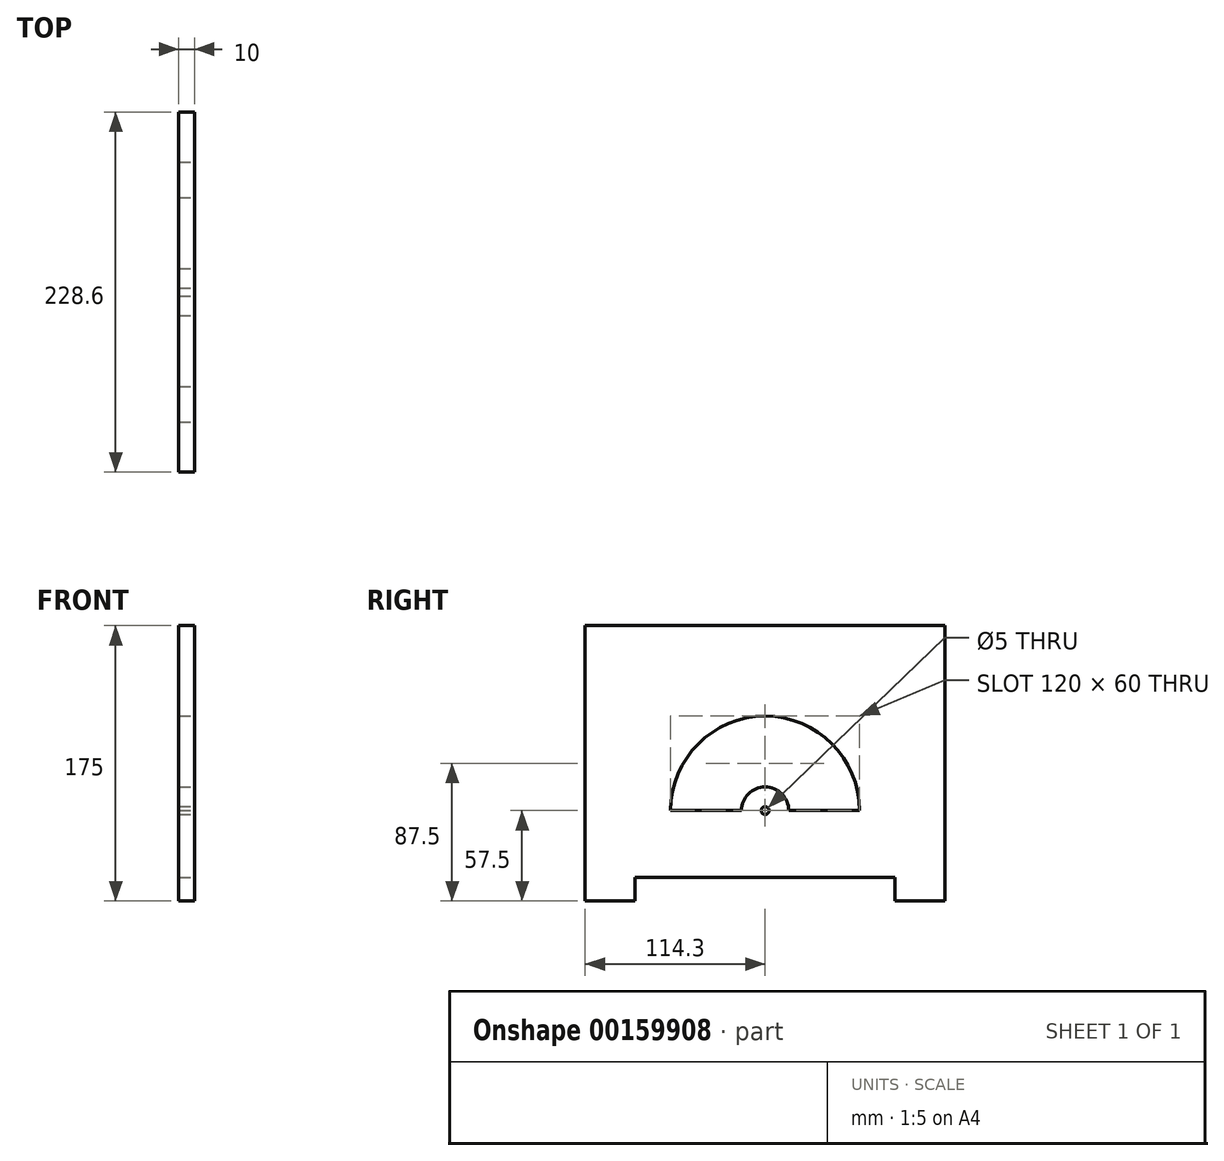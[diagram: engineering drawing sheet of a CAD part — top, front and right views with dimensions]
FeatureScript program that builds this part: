
annotation { "Feature Type Name" : "Feature", "Feature Type Description" : "" }
export const myFeature = defineFeature(function(context is Context, id is Id, definition is map)
    precondition{}
    {
        {
            var Q0;
            Q0=qCreatedBy(makeId("Right.planeOp"),FACE);
            var sketch = newSketch(context, id + "F0", { "sketchPlane" : qUnion([Q0])});
            skLineSegment(sketch, "E0.bottom", {"start": v(114.3, -87.5) * mm, "end": v(-114.3, -87.5) * mm});
            skLineSegment(sketch, "E0.top", {"start": v(114.3, 87.5) * mm, "end": v(-114.3, 87.5) * mm});
            skLineSegment(sketch, "E0.left", {"start": v(114.3, -87.5) * mm, "end": v(114.3, 87.5) * mm});
            skLineSegment(sketch, "E0.right", {"start": v(-114.3, -87.5) * mm, "end": v(-114.3, 87.5) * mm});
            skPoint(sketch, "E0.middle", {"position": v(0, 0) * mm});
            skSolve(sketch);
        }
        {
            var Q0;
            Q0=makeQuery(id+"F0.imprint","IMPRINT",FACE,{"disambiguationData":[TD([[makeQuery(id+"F0.imprint","IMPRINT",EDGE,{"derivedFrom":sQuery(id+"F0.wireOp",EDGE,"E0.bottom")}),-1.0]])]});
            extrude(context, id + "F1", {"entities" : qUnion([Q0]), "depth" : 10 * mm});
        }
        {
            var Q0;
            Q0=makeQuery(id+"F1.opExtrude","CAP_FACE",FACE,{"disambiguationData":[OSD([sQuery(id+"F0.wireOp",EDGE,"E0.bottom"),sQuery(id+"F0.wireOp",EDGE,"E0.top"),sQuery(id+"F0.wireOp",EDGE,"E0.left"),sQuery(id+"F0.wireOp",EDGE,"E0.right")])],"isStart":false});
            var sketch = newSketch(context, id + "F6", { "sketchPlane" : qUnion([Q0])});
            skSolve(sketch);
        }
        {
            var Q0;
            Q0=makeQuery(id+"F6.imprint","IMPRINT",FACE,{"disambiguationData":[TD([[makeQuery(id+"F6.imprint","IMPRINT",EDGE,{"derivedFrom":makeQuery(id+"F1.opExtrude","CAP_EDGE",EDGE,{"disambiguationData":[OSD([sQuery(id+"F0.wireOp",EDGE,"E0.bottom")])],"isStart":false})}),-1.0]])]});
            var sketch = newSketch(context, id + "F2", { "sketchPlane" : qUnion([Q0])});
            skLineSegment(sketch, "E1.bottom", {"start": v(60, 30) * mm, "end": v(-60, 30) * mm, "construction": true});
            skLineSegment(sketch, "E1.top", {"start": v(60, -30) * mm, "end": v(-60, -30) * mm, "construction": true});
            skLineSegment(sketch, "E1.left", {"start": v(60, 30) * mm, "end": v(60, -30) * mm, "construction": true});
            skLineSegment(sketch, "E1.right", {"start": v(-60, 30) * mm, "end": v(-60, -37.5) * mm, "construction": true});
            skPoint(sketch, "E1.middle", {"position": v(0, 0) * mm});
            skArc(sketch, "E2", {"start": v(60, -30) * mm, "mid": v(0, 30) * mm, "end": v(-60, -30) * mm});
            skLineSegment(sketch, "E3", {"start": v(0, -30) * mm, "end": v(0, -30) * mm});
            skLineSegment(sketch, "E4", {"start": v(-60, -30) * mm, "end": v(-15, -30) * mm});
            skArc(sketch, "E5", {"start": v(15, -30) * mm, "mid": v(0, -15) * mm, "end": v(-15, -30) * mm});
            skLineSegment(sketch, "E6.trimOffspring", {"start": v(15, -30) * mm, "end": v(60, -30) * mm});
            skSolve(sketch);
        }
        {
            var Q0;
            Q0 = qSketchRegion(id + "F2", true);
            extrude(context, id + "F7", {"entities" : qUnion([Q0]), "operationType" : NewBodyOperationType.REMOVE, "oppositeDirection" : true, "depth" : 25 * mm});
        }
        {
            var Q0;
            Q0=makeQuery(id+"F6.imprint","IMPRINT",FACE,{"disambiguationData":[TD([[makeQuery(id+"F6.imprint","IMPRINT",EDGE,{"derivedFrom":makeQuery(id+"F1.opExtrude","CAP_EDGE",EDGE,{"disambiguationData":[OSD([sQuery(id+"F0.wireOp",EDGE,"E0.bottom")])],"isStart":false})}),-1.0]])]});
            var sketch = newSketch(context, id + "F3", { "sketchPlane" : qUnion([Q0])});
            skLineSegment(sketch, "E7.bottom", {"start": v(82.5, -102.5) * mm, "end": v(-82.5, -102.5) * mm});
            skLineSegment(sketch, "E7.top", {"start": v(82.5, -72.5) * mm, "end": v(-82.5, -72.5) * mm});
            skLineSegment(sketch, "E7.left", {"start": v(82.5, -102.5) * mm, "end": v(82.5, -72.5) * mm});
            skLineSegment(sketch, "E7.right", {"start": v(-82.5, -102.5) * mm, "end": v(-82.5, -72.5) * mm});
            skPoint(sketch, "E7.middle", {"position": v(0, -87.5) * mm});
            skSolve(sketch);
        }
        {
            var Q0;
            Q0 = qSketchRegion(id + "F3", true);
            extrude(context, id + "F4", {"entities" : qUnion([Q0]), "operationType" : NewBodyOperationType.REMOVE, "oppositeDirection" : true, "depth" : 25 * mm});
        }
        {
            var Q0;
            Q0=makeQuery(id+"F6.imprint","IMPRINT",FACE,{"disambiguationData":[TD([[makeQuery(id+"F6.imprint","IMPRINT",EDGE,{"derivedFrom":makeQuery(id+"F1.opExtrude","CAP_EDGE",EDGE,{"disambiguationData":[OSD([sQuery(id+"F0.wireOp",EDGE,"E0.bottom")])],"isStart":false})}),-1.0]])]});
            var sketch = newSketch(context, id + "F8", { "sketchPlane" : qUnion([Q0])});
            skPoint(sketch, "E8", {"position": v(0, -30) * mm});
            skSolve(sketch);
        }
        {
            var Q0;
            Q0=sQuery(id+"F8.wireOp",VERTEX,"E8");
            var Q1;
            Q1=makeQuery(id+"F1.opExtrude","SWEPT_BODY",BODY,{"disambiguationData":[OSD([sQuery(id+"F0.wireOp",EDGE,"E0.bottom"),sQuery(id+"F0.wireOp",EDGE,"E0.top"),sQuery(id+"F0.wireOp",EDGE,"E0.left"),sQuery(id+"F0.wireOp",EDGE,"E0.right")])]});
            hole(context, id + "F9", {"style" : HoleStyle.SIMPLE, "endStyle" : HoleEndStyle.THROUGH, "holeDiameter" : 5 * mm, "locations" : qUnion([Q0]), "scope" : qUnion([Q1]), "isTappedThrough" : true});
        }
    });
